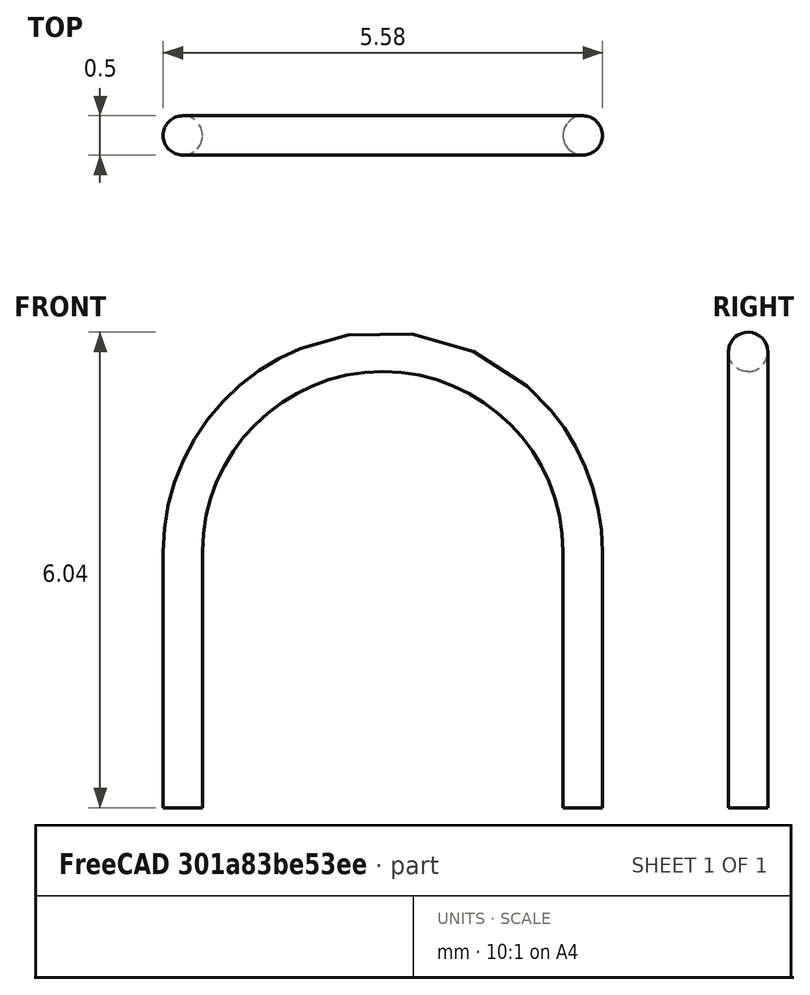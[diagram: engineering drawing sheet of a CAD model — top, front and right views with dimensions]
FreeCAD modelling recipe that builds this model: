
FCSTD DOCUMENT  (FreeCAD 0.17R12018 (Git))
Label: Test_Point_Bridge_Pitch5.08mm_Drill0.7mm
License: All rights reserved
LicenseURL: http://en.wikipedia.org/wiki/All_rights_reserved
objects: Sketcher::SketchObject×2, Spreadsheet::Sheet×1, PartDesign::SubtractivePipe×1, PartDesign::Body×1
note: 5 computed .brp shape members not serialized (recipe doc carries the construction recipe); baked Part::Feature solids carry a one-line shape summary decoded from their .brp

FEATURE [Sketcher::SketchObject] Sketch
  MapMode = 5
  Placement = pos=(0,0,-3) rot=(0,0,1;0rad)
  Support = -> [XY_Plane]
  superPlacement = pos=(0,0,-3) rot=(0,0,1;0rad)
  expr: Constraints[1] = dims.DWire / 2
  sketch-geometry (1):
    g0: Circle CenterX=0 CenterY=0 CenterZ=0 NormalX=0 NormalY=0 NormalZ=1 Radius=0.25
  constraints (2):
    c: Coincident(g0,g-1)
    c: Radius(g0) = 0.25
FEATURE [Spreadsheet::Sheet] Spreadsheet  label="dims"
  cells = A1="DWire"; B1(DWire)=0.5; A2="Pitch"; B2(Pitch)=5.0800000000000001
FEATURE [Sketcher::SketchObject] Sketch001
  MapMode = 5
  Placement = pos=(0,0,0) rot=(1,0,0;1.5708rad)
  Support = -> [XZ_Plane]
  expr: Constraints[10] = dims.DWire / 2
  expr: Constraints[3] = dims.Pitch
  sketch-geometry (4):
    g0: LineSegment StartX=0 StartY=-3 StartZ=0 EndX=0 EndY=0.25 EndZ=0
    g1: LineSegment StartX=5.08 StartY=0.25 StartZ=0 EndX=5.08 EndY=-3 EndZ=0
    g2: LineSegment [constr] StartX=0 StartY=0.25 StartZ=0 EndX=5.08 EndY=0.25 EndZ=0
    g3: ArcOfCircle CenterX=2.54 CenterY=0.25 CenterZ=0 NormalX=0 NormalY=0 NormalZ=1 Radius=2.54 StartAngle=0 EndAngle=3.14159
  constraints (13):
    c: PointOnObject(g0,g-2)
    c: Vertical(g0)
    c: Vertical(g1)
    c: DistanceX(g0,g1) = 5.08
    c: Coincident(g2,g0)
    c: Coincident(g2,g1)
    c: Horizontal(g2)
    c: PointOnObject(g3,g2)
    c: Coincident(g3,g0)
    c: Coincident(g3,g1)
    c: DistanceY(g-1,g3) = 0.25
    c: DistanceY(g0,g-1) = 3
    c: Equal(g1,g0)
FEATURE [PartDesign::SubtractivePipe] SubtractivePipe
  AuxilleryCurvelinear = true
  AuxillerySpineTangent = false
  Binormal = (0,0,0)
  Mode = 0
  Profile = -> Sketch
  Spine = -> Sketch001
  SpineTangent = false
  Transformation = 0
  Transition = 0
FEATURE [PartDesign::Body] Body  label="Test_Point_Bridge_Pitch5.08mm_Drill0.7mm"
  Group = -> [Sketch,Sketch001,SubtractivePipe]
  Origin = -> Origin
  Tip = -> SubtractivePipe
